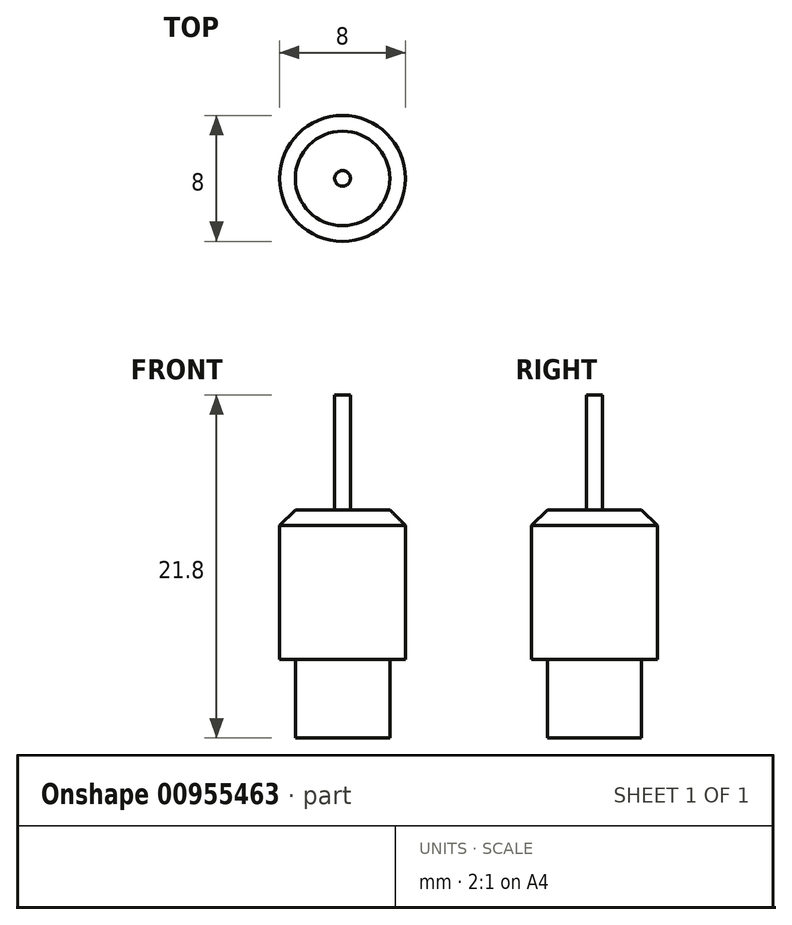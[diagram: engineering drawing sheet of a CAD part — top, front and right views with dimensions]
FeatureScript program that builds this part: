
annotation { "Feature Type Name" : "Feature", "Feature Type Description" : "" }
export const myFeature = defineFeature(function(context is Context, id is Id, definition is map)
    precondition{}
    {
        {
            var Q0;
            Q0=qCreatedBy(makeId("Front.planeOp"),FACE);
            var sketch = newSketch(context, id + "F0", { "sketchPlane" : qUnion([Q0])});
            skLineSegment(sketch, "E0", {"start": v(4, -16.8) * mm, "end": v(4, -8.3) * mm});
            skLineSegment(sketch, "E1", {"start": v(0.5, -7.3) * mm, "end": v(0.5, 0) * mm});
            skLineSegment(sketch, "E2", {"start": v(0.5, 0) * mm, "end": v(0, 0) * mm});
            skLineSegment(sketch, "E3", {"start": v(0, 0) * mm, "end": v(0, -21.8) * mm});
            skLineSegment(sketch, "E4", {"start": v(4, -16.8) * mm, "end": v(3, -16.8) * mm});
            skLineSegment(sketch, "E5", {"start": v(3, -16.8) * mm, "end": v(3, -21.8) * mm});
            skLineSegment(sketch, "E6", {"start": v(3, -21.8) * mm, "end": v(0, -21.8) * mm});
            skLineSegment(sketch, "E7", {"start": v(0.5, -7.3) * mm, "end": v(3, -7.3) * mm});
            skLineSegment(sketch, "E8", {"start": v(3, -7.3) * mm, "end": v(4, -8.3) * mm});
            skSolve(sketch);
        }
        {
            var Q0;
            Q0=qSketchRegion(id+"F0",true);
            var Q1;
            Q1=sQuery(id+"F0.wireOp",EDGE,"E3");
            revolve(context, id + "F1", {"surfaceOperationType" : NewSurfaceOperationType.NEW, "entities" : qUnion([Q0]), "axis" : qUnion([Q1]), "revolveType" : RevolveType.FULL});
        }
    });
